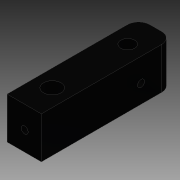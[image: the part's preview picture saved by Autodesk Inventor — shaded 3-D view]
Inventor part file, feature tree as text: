
AUTODESK INVENTOR PART (.ipt)
format: ipt  version: 2015 SP1 (Build 190203100, 203)  size: 122,368 bytes
history: native  units: in
note: dims shown in document units (in); Inventor stores cm internally (conversion verified against a paired STEP export)
features: hole x4, sketch x2, extrude x1
ambient origin geometry x8: Origin, YZ Plane, XZ Plane, XY Plane, X Axis, Y Axis, Z Axis, Center Point
bodies: Solid1 (feature_tree)
feature tree (7):
  extrude  "Extrusion1"  Depth=1.225in
  hole  "Hole1"  [1 undecoded]
  hole  "Hole3"  [1 undecoded]
  hole  "Hole4"  [1 undecoded]
  hole  "Hole5"  [1 undecoded]
  sketch  "Sketch1"  dims[d0=4.7in d1=1.225in]
  sketch  "Sketch2"  dims[d2=0.4in d3=0.625in d4=1.0in d5=1.485in d6=0.0in d7=1.0in d8=0.5in d9=0.75in d10=0.375in d11=0.25in d12=0.5635in d13=1.0in d14=0.8108in d24=1.0in d25=1.0in d26=0.25in d27=0.75in d28=0.375in d29=0.25in d30=0.5635in d31=0.5in d32=0.8108in d33=1.0in d34=1.0in d35=0.25in d36=0.75in d37=0.375in d38=0.25in d39=0.5635in d40=0.5in d41=0.8108in d42=1.0in d43=1.0in d44=0.25in d45=0.75in d46=0.375in d47=0.25in d48=0.5635in d49=0.5in d50=0.8108in]
note: 4 required parameter values undecoded (feature->parameter linkage not recoverable at this tier; creation-order binding heuristic only, values carry confidence <= 0.55)
